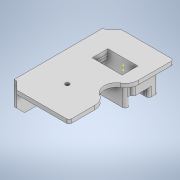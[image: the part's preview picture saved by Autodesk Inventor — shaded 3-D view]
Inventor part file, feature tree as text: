
AUTODESK INVENTOR PART (.ipt)
format: ipt  version: 2021 (Build 250183000, 183)  size: 288,768 bytes
history: native  units: mm
features: sketch x22, extrude x13, fillet x4, chamfer x2
ambient origin geometry x8: Origin, YZ Plane, XZ Plane, XY Plane, X Axis, Y Axis, Z Axis, Center Point
bodies: Body1 (feature_tree)
feature tree (41):
  extrude  "Extrusion3"  Depth=14.25mm TaperAngle=0.0deg
  sketch  "Sketch4"  dims[d7=35.0mm d8=12.0mm d9=0.0mm]
  extrude  "Extrusion4"  Depth=12.0mm TaperAngle=0.0deg
  sketch  "Sketch5"  dims[d10=15.0mm d11=4.0mm d12=0.0mm]
  sketch  "Sketch7"  dims[d35=80.0mm d36=3.0mm d37=0.0mm]
  extrude  "Extrusion5"  Depth=4.0mm TaperAngle=0.0deg
  sketch  "Sketch9"  dims[d41=5.0mm d42=0.0mm d43=7.0mm d44=0.0mm d45=2.0mm d46=2.0mm d47=6.0mm d48=2.0mm d49=45.0deg]
  sketch  "Sketch10"  dims[d50=3.0mm d51=23.2mm]
  extrude  "Extrusion9"  Depth=50.0mm
  extrude  "Extrusion10"  Depth=3.0mm TaperAngle=0.0deg
  extrude  "Extrusion11"  Depth=3.0mm TaperAngle=0.0deg
  extrude  "Extrusion12"  Depth=7.0mm TaperAngle=0.0deg
  fillet  "Fillet1"  Radius=2.0mm
  fillet  "Fillet2"  Radius=2.0mm
  sketch  "Sketch19"  dims[d69=2.0mm d70=10.0mm d71=0.0mm]
  chamfer  "Chamfer4"  Distance=6.0mm Angle=45.0deg
  sketch  "Sketch20"  dims[d72=10.0mm]
  extrude  "Extrusion13"  Depth=3.0mm
  sketch  "Sketch22"  dims[d78=2.0mm]
  sketch  "Sketch23"  dims[d79=10.0mm]
  extrude  "Extrusion14"  Depth=4.0mm TaperAngle=0.0deg
  chamfer  "Chamfer5"  Distance=2.0mm
  extrude  "Extrusion15"  Depth=2.0mm
  extrude  "Extrusion16"  Depth=4.0mm
  fillet  "Fillet3"  Radius=4.0mm
  extrude  "Extrusion17"  Depth=6.0mm
  fillet  "Fillet4"  Radius=2.152328mm
  extrude  "Extrusion19"  Depth=10.0mm TaperAngle=0.0deg
  sketch  "Sketch3"  dims[d4=2.0mm d5=14.25mm d6=0.0mm]
  sketch  "Sketch6"  dims[d33=11.005905mm d34=50.0mm]
  sketch  "Sketch8"  dims[d38=5.8mm d39=3.0mm d40=0.0mm]
  sketch  "Sketch15"  dims[d52=21.45mm d53=4.0mm d54=0.0mm d55=2.0mm d56=0.0mm]
  sketch  "Sketch16"  dims[d57=6.0mm d58=2.0mm d59=45.0deg d60=2.0mm]
  sketch  "Sketch17"  dims[d61=2.4mm d62=6.2mm d63=4.0mm d64=0.0mm]
  sketch  "Sketch18"  dims[d65=4.0mm d66=0.0mm d67=6.0mm d68=2.152328mm]
  sketch  "Sketch21"  dims[d77=2.0mm]
  sketch  "Sketch24"  dims[d80=24.0mm]
  sketch  "Sketch25"  dims[d81=10.0mm d82=0.0mm]
  sketch  "Sketch26"  dims[d26=0.5mm]
  sketch  "Sketch27"  dims[d27=0.872665mm]
  sketch  "Sketch29"  dims[d28=0.5mm d29=0.872665mm d30=0.5mm d31=0.872665mm d83=0.872665mm]
